# Revit family: Bright 5.G
name_source: partatom
category: Lighting Fixtures
revit_build: Autodesk Revit 2017 (Build: 20170419_0315(x64)
units: mm (PartAtom-declared; Revit-internal decimal feet)

## family parameters
Cut with Voids When Loaded = Yes
Host = Face
Light Source = Yes
Part Type = Normal
Room Calculation Point = Yes
Round Connector Dimension = Use Diameter
Shared = No

## types (8) — shared parameters
Apparent Load = 0 VA
Body = L&L_Anodized aluminium
CRI = 90 (also available: CRI 80 - ref. URL Technical sheet)
Code = -
Color Filter = 16777215
Control system = -
Cutout dimensions = diam. 125 mm
Default Elevation = 1219 mm
Delivered lumen output = 816 lm (3000K, 10W, 55°, CRI 80), 686 lm (3000K, 10W, 55°, CRI 90), 1235 lm (3000K, 16W, 55°, CRI 80), 1037 lm (3000K, 16W, 55°, CRI 90)
Description = recessed for outdoor applications
Dimming Lamp Color Temperature Shift = <None>
Emit from Line Length = 610 mm
Energy efficiency class = A A+ A++
Geometry = Bright 5.G_mod
Height Void = 110 mm  [stored 0.360892 ft]
Height mm = 107 mm  [stored 0.35105 ft]
IP = IP67
LED Colour = 3000K (also available: 2700K and 4000K - ref. URL Technical sheet)
Length mm = 148 mm  [stored 0.485564 ft]
Lens = L&L_Tempered extra-clear glass
Lumen output at source = 868 lm (3000K, 10W, CRI 90), 1564 lm (3000K, 16W, CRI 80), 1313 lm (3000K, 16W, CRI 90), 1033 lm (3000K, 10W, CRI 80)
Manufacturer = L&L Luce&Light
Material = body in anodized aluminium, trim in AISI 316L stainless steel, screen in tempered, serigraphed-grey and transparent extra-clear glass
Model = Bright 5.G
Mounting = recessed (ceiling, wall, floor)
No. and type of led = 1 high power density COB LED, 3-step MacAdam, 50 000h L90 B10 (Ta 25°C)
Notes = -
Power Supply = L&L_Steel inox AISI 316L
Power cables = includes 1,50 m neoprene cable, H05RN-F 2x0,75/0,75 Ø6,3 mm
Power supply = 24Vdc
Power supply unit = not included
Radius Void = 65 mm  [stored 0.213255 ft]
Tilt Angle = 90.00°
Tiltable = ±10°
Trim = L&L_Steel inox AISI 316L
URL = https://www.lucelight.it
URL Accessories and power supply units = https://www.lucelight.it
URL Catalogue = https://www.lucelight.it
URL DXF = https://www.lucelight.it
URL Description = https://www.lucelight.it
URL General code = https://www.lucelight.it
URL IES Photometric file = https://www.lucelight.it
URL Image = https://www.lucelight.it
URL Technical sheet = https://www.lucelight.it
Voltage = 24 V
Weight kg = 1.65 kg
Width mm = 148 mm  [stored 0.485564 ft]
Wiring = parallel

## per-type parameters (varying)
| type | Apparent Load Phase 1 | Optics | Photometric Web File | Power |
| Bright 5.G K 55° (3000K 10W 24Vdc) | 10 W | 55° tiltable ±10° | BRIGHT 5.G K 55° [3000K 10W 24Vdc].IES | 10W |
| Bright 5.G L 38° (3000K 10W 24Vdc) | 10 W | 38° tiltable ±10° | BRIGHT 5.G L 38° [3000K 10W 24Vdc].IES | 10W |
| Bright 5.G M 31° (3000K 10W 24Vdc) | 10 W | 31° tiltable ±10° | BRIGHT 5.G M 31° [3000K 10W 24Vdc].IES | 10W |
| Bright 5.G S 12° (3000K 10W 24Vdc) | 10 W | 12° tiltable ±10° | BRIGHT 5.G S 12° [3000K 10W 24Vdc].IES | 10W |
| Bright 5.G K 55° (3000K 16W 24Vdc) | 16 W | 55° tiltable ±10° | BRIGHT 5.G K 55° [3000K 16W 24Vdc].IES | 16W |
| Bright 5.G L 38° (3000K 16W 24Vdc) | 16 W | 38° tiltable ±10° | BRIGHT 5.G L 38° [3000K 16W 24Vdc].IES | 16W |
| Bright 5.G M 31° (3000K 16W 24Vdc) | 16 W | 31° tiltable ±10° | BRIGHT 5.G M 31° [3000K 16W 24Vdc].IES | 16W |
| Bright 5.G S 12° (3000K 16W 24Vdc) | 16 W | 12° tiltable ±10° | BRIGHT 5.G S 12° [3000K 16W 24Vdc].IES | 16W |

note: [stored X ft] marks values corroborated as IEEE doubles in the binary element streams (Revit-internal decimal feet)

## geometry (parser evidence)
native form markers: Blend x2, Sweep x7
no freeform markers — native parametric forms only
